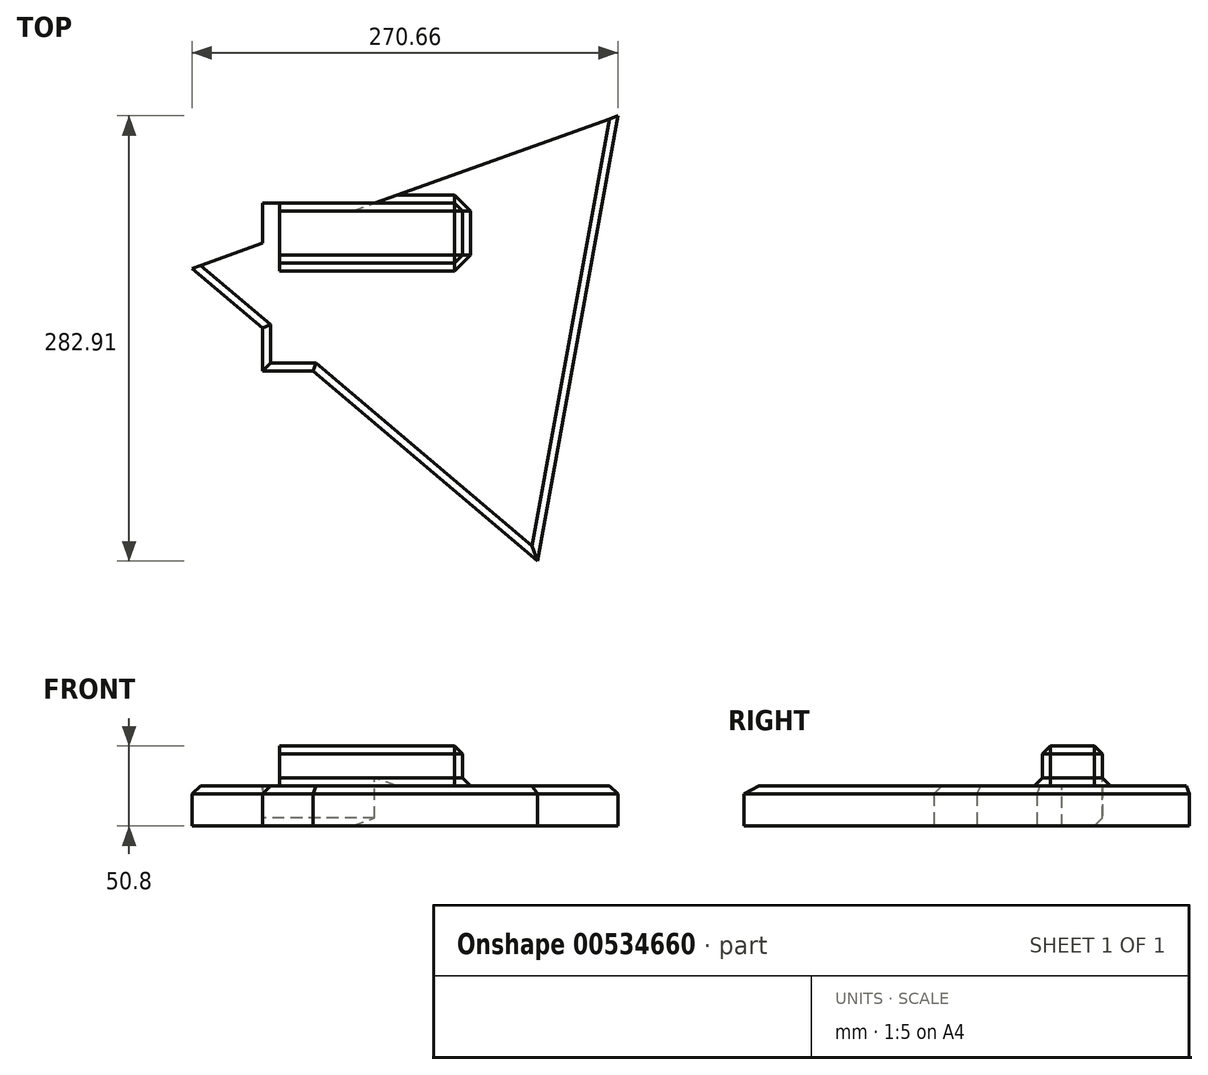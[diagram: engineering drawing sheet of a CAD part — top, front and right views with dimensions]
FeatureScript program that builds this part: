
annotation { "Feature Type Name" : "Feature", "Feature Type Description" : "" }
export const myFeature = defineFeature(function(context is Context, id is Id, definition is map)
    precondition{}
    {
        {
            var Q0;
            Q0=qCreatedBy(makeId("Top.planeOp"),FACE);
            var sketch = newSketch(context, id + "F0", { "sketchPlane" : qUnion([Q0])});
            skLineSegment(sketch, "E0.bottom", {"start": v(-59.58, 38.1) * mm, "end": v(67.42, 38.1) * mm});
            skLineSegment(sketch, "E0.top", {"start": v(-59.58, 0) * mm, "end": v(67.42, 0) * mm});
            skLineSegment(sketch, "E0.left", {"start": v(-59.58, 38.1) * mm, "end": v(-59.58, 0) * mm});
            skLineSegment(sketch, "E0.right", {"start": v(67.42, 38.1) * mm, "end": v(67.42, 0) * mm});
            skSolve(sketch);
        }
        {
            var Q0;
            Q0=makeQuery(id+"F0.imprint","IMPRINT",FACE,{"disambiguationData":[TD([[makeQuery(id+"F0.imprint","IMPRINT",EDGE,{"derivedFrom":sQuery(id+"F0.wireOp",EDGE,"E0.bottom")}),-1.0]])]});
            extrude(context, id + "F1", {"entities" : qUnion([Q0]), "depth" : 25.4 * mm, "offsetDistance" : 25.4 * mm});
        }
        {
            var Q0;
            Q0=makeQuery(id+"F1.opExtrude","CAP_FACE",FACE,{"disambiguationData":[OSD([sQuery(id+"F0.wireOp",EDGE,"E0.bottom"),sQuery(id+"F0.wireOp",EDGE,"E0.top"),sQuery(id+"F0.wireOp",EDGE,"E0.left"),sQuery(id+"F0.wireOp",EDGE,"E0.right")])],"isStart":false});
            var sketch = newSketch(context, id + "F2", { "sketchPlane" : qUnion([Q0])});
            skLineSegment(sketch, "E1.bottom", {"start": v(-48.51, 38.1) * mm, "end": v(67.42, 38.1) * mm});
            skLineSegment(sketch, "E1.top", {"start": v(-48.51, 0) * mm, "end": v(67.42, 0) * mm});
            skLineSegment(sketch, "E1.left", {"start": v(-48.51, 38.1) * mm, "end": v(-48.51, 0) * mm});
            skLineSegment(sketch, "E1.right", {"start": v(67.42, 38.1) * mm, "end": v(67.42, 0) * mm});
            skSolve(sketch);
        }
        {
            var Q0;
            Q0=makeQuery(id+"F2.imprint","IMPRINT",FACE,{"disambiguationData":[TD([[makeQuery(id+"F2.imprint","IMPRINT",EDGE,{"derivedFrom":sQuery(id+"F2.wireOp",EDGE,"E1.bottom")}),-1.0]])]});
            extrude(context, id + "F3", {"entities" : qUnion([Q0]), "operationType" : NewBodyOperationType.ADD, "depth" : 25.4 * mm, "offsetDistance" : 25.4 * mm});
        }
        {
            var Q0;
            Q0=qCreatedBy(makeId("Top.planeOp"),FACE);
            var sketch = newSketch(context, id + "F4", { "sketchPlane" : qUnion([Q0])});
            skLineSegment(sketch, "E2.bottom", {"start": v(-59.52, 0) * mm, "end": v(67.48, 0) * mm});
            skLineSegment(sketch, "E2.top", {"start": v(-59.52, -68.65) * mm, "end": v(67.48, -68.65) * mm});
            skLineSegment(sketch, "E2.left", {"start": v(-59.52, 0) * mm, "end": v(-59.52, -68.65) * mm});
            skLineSegment(sketch, "E2.right", {"start": v(67.48, 0) * mm, "end": v(67.48, -68.65) * mm});
            skSolve(sketch);
        }
        {
            var Q0;
            Q0=makeQuery(id+"F4.imprint","IMPRINT",FACE,{"disambiguationData":[TD([[makeQuery(id+"F4.imprint","IMPRINT",EDGE,{"derivedFrom":sQuery(id+"F4.wireOp",EDGE,"E2.bottom")}),-1.0]])]});
            extrude(context, id + "F5", {"entities" : qUnion([Q0]), "operationType" : NewBodyOperationType.ADD, "depth" : 25.4 * mm, "offsetDistance" : 25.4 * mm});
        }
        {
            var Q0;
            Q0=qCreatedBy(makeId("Top.planeOp"),FACE);
            var sketch = newSketch(context, id + "F6", { "sketchPlane" : qUnion([Q0])});
            skCircle(sketch, "E3.cCircle", {"center": v(59.05, -33.14) * mm, "radius": 83 * mm, "construction": true});
            skLineSegment(sketch, "E3.0", {"start": v(166.37, 93.5) * mm, "end": v(115.07, -189.4) * mm});
            skLineSegment(sketch, "E3.1", {"start": v(115.07, -189.4) * mm, "end": v(-104.29, -3.52) * mm});
            skLineSegment(sketch, "E3.2", {"start": v(-104.29, -3.52) * mm, "end": v(166.37, 93.5) * mm});
            skPoint(sketch, "E3.0.midPoint", {"position": v(140.72, -47.95) * mm});
            skSolve(sketch);
        }
        {
            var Q0;
            Q0=makeQuery(id+"F6.imprint","IMPRINT",FACE,{"disambiguationData":[TD([[makeQuery(id+"F6.imprint","IMPRINT",EDGE,{"derivedFrom":sQuery(id+"F6.wireOp",EDGE,"E3.0")}),-1.0]])]});
            extrude(context, id + "F7", {"entities" : qUnion([Q0]), "operationType" : NewBodyOperationType.ADD, "depth" : 25.4 * mm, "offsetDistance" : 25.4 * mm});
        }
        {
            var Q0;
            Q0=makeQuery(id+"F7.opExtrude","CAP_EDGE",EDGE,{"disambiguationData":[OSD([sQuery(id+"F6.wireOp",EDGE,"E3.0")])],"isStart":false});
            var Q1;
            {var subQ1=sQuery(id+"F4.wireOp",EDGE,"E2.top");var subQ2=sQuery(id+"F6.wireOp",EDGE,"E3.1");Q1=makeQuery(id+"F7.boolean.opBoolean","SPLIT",EDGE,{"disambiguationData":[TD([makeQuery(id+"F5.opExtrude","SWEPT_FACE",FACE,{"disambiguationData":[OSD([subQ1])]})])],"derivedFrom":makeQuery(id+"F7.opExtrude","CAP_EDGE",EDGE,{"disambiguationData":[OSD([subQ2])],"isStart":false})});}
            var Q2;
            Q2=makeQuery(id+"F5.opExtrude","CAP_EDGE",EDGE,{"disambiguationData":[OSD([sQuery(id+"F4.wireOp",EDGE,"E2.top")])],"isStart":false});
            var Q3;
            Q3=makeQuery(id+"F5.opExtrude","CAP_EDGE",EDGE,{"disambiguationData":[OSD([sQuery(id+"F4.wireOp",EDGE,"E2.left")])],"isStart":false});
            var Q4;
            {var subQ1=sQuery(id+"F6.wireOp",EDGE,"E3.1");var subQ2=sQuery(id+"F4.wireOp",EDGE,"E2.left");Q4=makeQuery(id+"F7.boolean.opBoolean","SPLIT",EDGE,{"disambiguationData":[TD([makeQuery(id+"F5.opExtrude","SWEPT_FACE",FACE,{"disambiguationData":[OSD([subQ2])]})])],"derivedFrom":makeQuery(id+"F7.opExtrude","CAP_EDGE",EDGE,{"disambiguationData":[OSD([subQ1])],"isStart":false})});}
            var Q5;
            Q5=makeQuery(id+"F3.opExtrude","CAP_EDGE",EDGE,{"disambiguationData":[OSD([sQuery(id+"F2.wireOp",EDGE,"E1.top")])],"isStart":false});
            var Q6;
            Q6=makeQuery(id+"F1.opExtrude","CAP_EDGE",EDGE,{"disambiguationData":[OSD([sQuery(id+"F0.wireOp",EDGE,"E0.bottom")])],"isStart":true});
            var Q7;
            Q7=makeQuery(id+"F3.opExtrude","CAP_EDGE",EDGE,{"disambiguationData":[OSD([sQuery(id+"F2.wireOp",EDGE,"E1.bottom")])],"isStart":false});
            var Q8;
            Q8=makeQuery(id+"F3.opExtrude","CAP_EDGE",EDGE,{"disambiguationData":[OSD([sQuery(id+"F2.wireOp",EDGE,"E1.right")])],"isStart":false});
            var Q9;
            Q9=makeQuery(id+"F3.boolean.opBoolean","MERGE",FACE,{"derivedFrom":[makeQuery(id+"F1.opExtrude","SWEPT_FACE",FACE,{"disambiguationData":[OSD([sQuery(id+"F0.wireOp",EDGE,"E0.right")])]}),makeQuery(id+"F3.opExtrude","SWEPT_FACE",FACE,{"disambiguationData":[OSD([sQuery(id+"F2.wireOp",EDGE,"E1.right")])]})]});
            chamfer(context, id + "F8", {"entities" : qUnion([Q0, Q1, Q2, Q3, Q4, Q5, Q6, Q7, Q8, Q9]), "width" : 5.08 * mm, "tangentPropagation" : true});
        }
        {
            var Q0;
            Q0=qCreatedBy(makeId("Top.planeOp"),FACE);
            var sketch = newSketch(context, id + "F9", { "sketchPlane" : qUnion([Q0])});
            skEllipse(sketch, "E4", {"center": v(23.43, -31.63) * mm, "majorRadius": 46.86 * mm, "minorRadius": 21.69 * mm, "majorAxis": v(1, 0)});
            skSolve(sketch);
        }
        {
            var Q0;
            Q0=sQuery(id+"F9.wireOp",EDGE,"E4");
            extrude(context, id + "F10", {"bodyType" : ToolBodyType.SURFACE, "surfaceEntities" : qUnion([Q0]), "depth" : 76.2 * mm, "offsetDistance" : 25.4 * mm});
        }
    });
